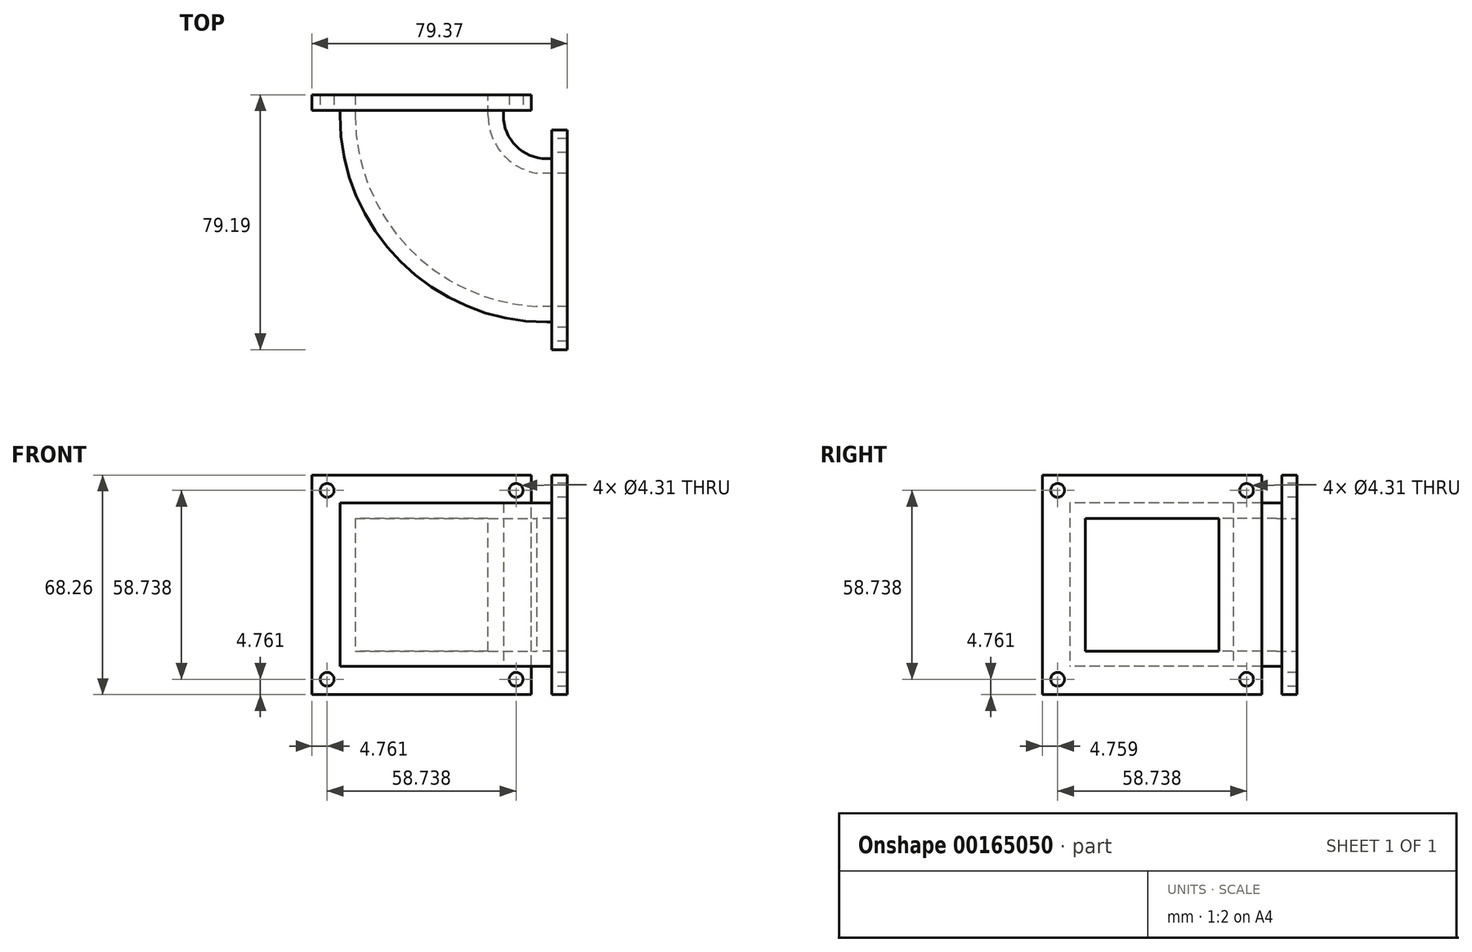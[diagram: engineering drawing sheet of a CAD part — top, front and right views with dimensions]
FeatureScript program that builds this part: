
annotation { "Feature Type Name" : "Feature", "Feature Type Description" : "" }
export const myFeature = defineFeature(function(context is Context, id is Id, definition is map)
    precondition{}
    {
        {
            var Q0;
            Q0=qCreatedBy(makeId("Top.planeOp"),FACE);
            var sketch = newSketch(context, id + "F0", { "sketchPlane" : qUnion([Q0])});
            skLineSegment(sketch, "E0", {"start": v(0, 0) * mm, "end": v(0, 1.59) * mm});
            skLineSegment(sketch, "E1", {"start": v(0, 1.59) * mm, "end": v(-50.8, 1.59) * mm});
            skLineSegment(sketch, "E2", {"start": v(-50.8, 1.59) * mm, "end": v(-50.8, 0) * mm});
            skLineSegment(sketch, "E3", {"start": v(-50.8, 0) * mm, "end": v(0, 0) * mm, "construction": true});
            skArc(sketch, "E4", {"start": v(0, 0) * mm, "mid": v(3.95, -9.54) * mm, "end": v(13.5, -13.5) * mm});
            skArc(sketch, "E5", {"start": v(-50.8, 0) * mm, "mid": v(-31.97, -45.46) * mm, "end": v(13.5, -64.3) * mm});
            skLineSegment(sketch, "E6.bottom", {"start": v(13.5, -13.5) * mm, "end": v(15.08, -13.5) * mm});
            skLineSegment(sketch, "E6.top", {"start": v(13.5, -64.3) * mm, "end": v(15.08, -64.3) * mm});
            skLineSegment(sketch, "E6.left", {"start": v(13.5, -13.5) * mm, "end": v(13.5, -64.3) * mm, "construction": true});
            skLineSegment(sketch, "E6.right", {"start": v(15.08, -13.5) * mm, "end": v(15.08, -64.3) * mm});
            skLineSegment(sketch, "E7", {"start": v(15.08, -13.5) * mm, "end": v(15.08, 1.59) * mm, "construction": true});
            skLineSegment(sketch, "E8", {"start": v(15.08, 1.59) * mm, "end": v(0, 1.59) * mm, "construction": true});
            skPoint(sketch, "E9", {"position": v(15.08, -38.9) * mm});
            skSolve(sketch);
        }
        {
            var Q0;
            Q0 = qSketchRegion(id + "F0", true);
            extrude(context, id + "F1", {"entities" : qUnion([Q0]), "depth" : 50.8 * mm});
        }
        {
            var Q0;
            Q0=makeQuery(id+"F1.opExtrude","SWEPT_FACE",FACE,{"disambiguationData":[OSD([sQuery(id+"F0.wireOp",EDGE,"E1")])]});
            shell(context, id + "F2", {"entities" : qUnion([Q0]), "thickness" : 4.76 * mm});
        }
        {
            var Q0;
            Q0=makeQuery(id+"F2.opShell","OFFSET_FACE",FACE,{"disambiguationData":[OSD([sQuery(id+"F0.wireOp",EDGE,"E6.right")])]});
            var Q1;
            Q1=makeQuery(id+"F1.opExtrude","SWEPT_FACE",FACE,{"disambiguationData":[OSD([sQuery(id+"F0.wireOp",EDGE,"E6.right")])]});
            extrude(context, id + "F3", {"entities" : qUnion([Q0]), "operationType" : NewBodyOperationType.REMOVE, "endBound" : BoundingType.UP_TO_SURFACE, "oppositeDirection" : true, "endBoundEntityFace" : qUnion([Q1]), "depth" : 25.4 * mm});
        }
        {
            var Q0;
            Q0=makeQuery(id+"F1.opExtrude","SWEPT_FACE",FACE,{"disambiguationData":[OSD([sQuery(id+"F0.wireOp",EDGE,"E6.right")])]});
            var sketch = newSketch(context, id + "F4", { "sketchPlane" : qUnion([Q0])});
            skLineSegment(sketch, "E10.bottom", {"start": v(-68.08, -3.97) * mm, "end": v(-9.34, -3.97) * mm, "construction": true});
            skLineSegment(sketch, "E10.top", {"start": v(-68.08, 54.77) * mm, "end": v(-9.34, 54.77) * mm, "construction": true});
            skLineSegment(sketch, "E10.left", {"start": v(-68.08, -3.97) * mm, "end": v(-68.08, 54.77) * mm, "construction": true});
            skLineSegment(sketch, "E10.right", {"start": v(-9.34, -3.97) * mm, "end": v(-9.34, 54.77) * mm, "construction": true});
            skPoint(sketch, "E10.middle", {"position": v(-38.71, 25.4) * mm});
            skLineSegment(sketch, "E11.bottom", {"start": v(-72.84, -8.73) * mm, "end": v(-4.58, -8.73) * mm});
            skLineSegment(sketch, "E11.top", {"start": v(-72.84, 59.53) * mm, "end": v(-4.58, 59.53) * mm});
            skLineSegment(sketch, "E11.left", {"start": v(-72.84, -8.73) * mm, "end": v(-72.84, 59.53) * mm});
            skLineSegment(sketch, "E11.right", {"start": v(-4.58, -8.73) * mm, "end": v(-4.58, 59.53) * mm});
            skLineSegment(sketch, "E12", {"start": v(-68.08, -3.97) * mm, "end": v(-68.08, -8.73) * mm, "construction": true});
            skLineSegment(sketch, "E13", {"start": v(-68.08, -3.97) * mm, "end": v(-72.84, -3.97) * mm, "construction": true});
            skLineSegment(sketch, "E14", {"start": v(-72.84, -8.73) * mm, "end": v(-68.08, -3.97) * mm, "construction": true});
            skCircle(sketch, "E15", {"center": v(-9.34, -3.97) * mm, "radius": 2.15 * mm});
            skCircle(sketch, "E16", {"center": v(-68.08, -3.97) * mm, "radius": 2.15 * mm});
            skCircle(sketch, "E17", {"center": v(-68.08, 54.77) * mm, "radius": 2.15 * mm});
            skCircle(sketch, "E18", {"center": v(-9.34, 54.77) * mm, "radius": 2.15 * mm});
            skLineSegment(sketch, "E19.bottom", {"start": v(-17.98, 4.76) * mm, "end": v(-59.45, 4.76) * mm});
            skLineSegment(sketch, "E19.top", {"start": v(-17.98, 46.04) * mm, "end": v(-59.45, 46.04) * mm});
            skLineSegment(sketch, "E19.left", {"start": v(-17.98, 4.76) * mm, "end": v(-17.98, 46.04) * mm});
            skLineSegment(sketch, "E19.right", {"start": v(-59.45, 4.76) * mm, "end": v(-59.45, 46.04) * mm});
            skSolve(sketch);
        }
        {
            var Q0;
            Q0=makeQuery(id+"F4.imprint","IMPRINT",FACE,{"disambiguationData":[TD([[makeQuery(id+"F4.imprint","IMPRINT",EDGE,{"derivedFrom":sQuery(id+"F4.wireOp",EDGE,"RLEXA1B5-z5ns-qXUs-1C0E-BimdxLFVxaIm.bottom")}),1.0]])]});
            var Q1;
            Q1=makeQuery(id+"F4.imprint","IMPRINT",FACE,{"disambiguationData":[TD([[makeQuery(id+"F4.imprint","IMPRINT",EDGE,{"derivedFrom":sQuery(id+"F4.wireOp",EDGE,"E11.bottom")}),1.0]])]});
            var Q2;
            Q2=makeQuery(id+"F4.imprint","IMPRINT",FACE,{"disambiguationData":[TD([[makeQuery(id+"F4.imprint","IMPRINT",EDGE,{"derivedFrom":sQuery(id+"F4.wireOp",EDGE,"E19.bottom")}),1.0]])]});
            extrude(context, id + "F5", {"entities" : qUnion([Q0, Q1, Q2]), "operationType" : NewBodyOperationType.ADD, "depth" : 4.76 * mm});
        }
        {
            var Q0;
            Q0=makeQuery(id+"F1.opExtrude","SWEPT_FACE",FACE,{"disambiguationData":[OSD([sQuery(id+"F0.wireOp",EDGE,"E1")])]});
            var sketch = newSketch(context, id + "F6", { "sketchPlane" : qUnion([Q0])});
            skLineSegment(sketch, "E20.bottom", {"start": v(46.04, 46.04) * mm, "end": v(4.76, 46.04) * mm});
            skLineSegment(sketch, "E20.top", {"start": v(46.04, 4.76) * mm, "end": v(4.76, 4.76) * mm});
            skLineSegment(sketch, "E20.left", {"start": v(46.04, 46.04) * mm, "end": v(46.04, 4.76) * mm});
            skLineSegment(sketch, "E20.right", {"start": v(4.76, 46.04) * mm, "end": v(4.76, 4.76) * mm});
            skLineSegment(sketch, "E21", {"start": v(46.04, 25.4) * mm, "end": v(4.76, 25.4) * mm, "construction": true});
            skLineSegment(sketch, "E22.bottom", {"start": v(59.53, -8.73) * mm, "end": v(-8.73, -8.73) * mm});
            skLineSegment(sketch, "E22.top", {"start": v(59.53, 59.53) * mm, "end": v(-8.73, 59.53) * mm});
            skLineSegment(sketch, "E22.left", {"start": v(59.53, -8.73) * mm, "end": v(59.53, 59.53) * mm});
            skLineSegment(sketch, "E22.right", {"start": v(-8.73, -8.73) * mm, "end": v(-8.73, 59.53) * mm});
            skPoint(sketch, "E22.middle", {"position": v(25.4, 25.4) * mm});
            skLineSegment(sketch, "E23.bottom", {"start": v(54.77, -3.97) * mm, "end": v(-3.97, -3.97) * mm, "construction": true});
            skLineSegment(sketch, "E23.top", {"start": v(54.77, 54.77) * mm, "end": v(-3.97, 54.77) * mm, "construction": true});
            skLineSegment(sketch, "E23.left", {"start": v(54.77, -3.97) * mm, "end": v(54.77, 54.77) * mm, "construction": true});
            skLineSegment(sketch, "E23.right", {"start": v(-3.97, -3.97) * mm, "end": v(-3.97, 54.77) * mm, "construction": true});
            skLineSegment(sketch, "E24", {"start": v(54.77, -3.97) * mm, "end": v(59.53, -3.97) * mm, "construction": true});
            skLineSegment(sketch, "E25", {"start": v(25.4, -3.97) * mm, "end": v(25.4, 0) * mm, "construction": true});
            skLineSegment(sketch, "E26", {"start": v(25.4, -3.97) * mm, "end": v(25.4, -8.73) * mm, "construction": true});
            skCircle(sketch, "E27", {"center": v(-3.97, 54.77) * mm, "radius": 2.15 * mm});
            skCircle(sketch, "E28", {"center": v(54.77, 54.77) * mm, "radius": 2.15 * mm});
            skCircle(sketch, "E29", {"center": v(54.77, -3.97) * mm, "radius": 2.15 * mm});
            skCircle(sketch, "E30", {"center": v(-3.97, -3.97) * mm, "radius": 2.15 * mm});
            skSolve(sketch);
        }
        {
            var Q0;
            Q0 = qSketchRegion(id + "F6", true);
            extrude(context, id + "F7", {"entities" : qUnion([Q0]), "operationType" : NewBodyOperationType.ADD, "depth" : 4.76 * mm});
        }
        {
            var Q0;
            Q0=makeQuery(id+"F5.opExtrude","CAP_FACE",FACE,{"disambiguationData":[OSD([sQuery(id+"F4.wireOp",EDGE,"RLEXA1B5-z5ns-qXUs-1C0E-BimdxLFVxaIm.bottom"),sQuery(id+"F4.wireOp",EDGE,"RLEXA1B5-z5ns-qXUs-1C0E-BimdxLFVxaIm.top"),sQuery(id+"F4.wireOp",EDGE,"RLEXA1B5-z5ns-qXUs-1C0E-BimdxLFVxaIm.left"),sQuery(id+"F4.wireOp",EDGE,"RLEXA1B5-z5ns-qXUs-1C0E-BimdxLFVxaIm.right"),sQuery(id+"F4.wireOp",EDGE,"E11.bottom"),sQuery(id+"F4.wireOp",EDGE,"E11.top"),sQuery(id+"F4.wireOp",EDGE,"E11.left"),sQuery(id+"F4.wireOp",EDGE,"E11.right"),sQuery(id+"F4.wireOp",EDGE,"E15"),sQuery(id+"F4.wireOp",EDGE,"E16"),sQuery(id+"F4.wireOp",EDGE,"E17"),sQuery(id+"F4.wireOp",EDGE,"E18")])],"isStart":true});
            var sketch = newSketch(context, id + "F8", { "sketchPlane" : qUnion([Q0])});
            skCircle(sketch, "E31", {"center": v(68.08, 54.77) * mm, "radius": 4.76 * mm});
            skSolve(sketch);
        }
        {
            var Q0;
            {var subQ5=sQuery(id+"F4.wireOp",EDGE,"E17");var subQ14=makeQuery(id+"F5.boolean.opBoolean","SPLIT",EDGE,{"disambiguationData":[OD(0.0)],"derivedFrom":makeQuery(id+"F5.opExtrude","CAP_EDGE",EDGE,{"disambiguationData":[OSD([subQ5])],"isStart":true})});Q0=makeQuery(id+"F8.imprint","IMPRINT",FACE,{"disambiguationData":[TD([[makeQuery(id+"F8.imprint","IMPRINT",EDGE,{"derivedFrom":subQ14}),1.0]])]});}
            var Q1;
            {var subQ1=sQuery(id+"F4.wireOp",EDGE,"E17");var subQ13=makeQuery(id+"F5.boolean.opBoolean","SPLIT",EDGE,{"disambiguationData":[OD(0.0)],"derivedFrom":makeQuery(id+"F5.opExtrude","CAP_EDGE",EDGE,{"disambiguationData":[OSD([subQ1])],"isStart":true})});Q1=makeQuery(id+"F8.imprint","IMPRINT",FACE,{"disambiguationData":[TD([[makeQuery(id+"F8.imprint","IMPRINT",EDGE,{"derivedFrom":subQ13}),-1.0]])]});}
            var Q2;
            Q2=makeQuery(id+"F1.opExtrude","SWEPT_FACE",FACE,{"disambiguationData":[OSD([sQuery(id+"F0.wireOp",EDGE,"E5")])]});
            extrude(context, id + "F9", {"entities" : qUnion([Q0, Q1]), "operationType" : NewBodyOperationType.REMOVE, "endBound" : BoundingType.THROUGH_ALL, "endBoundEntityFace" : qUnion([Q2]), "depth" : 25.4 * mm});
        }
    });
